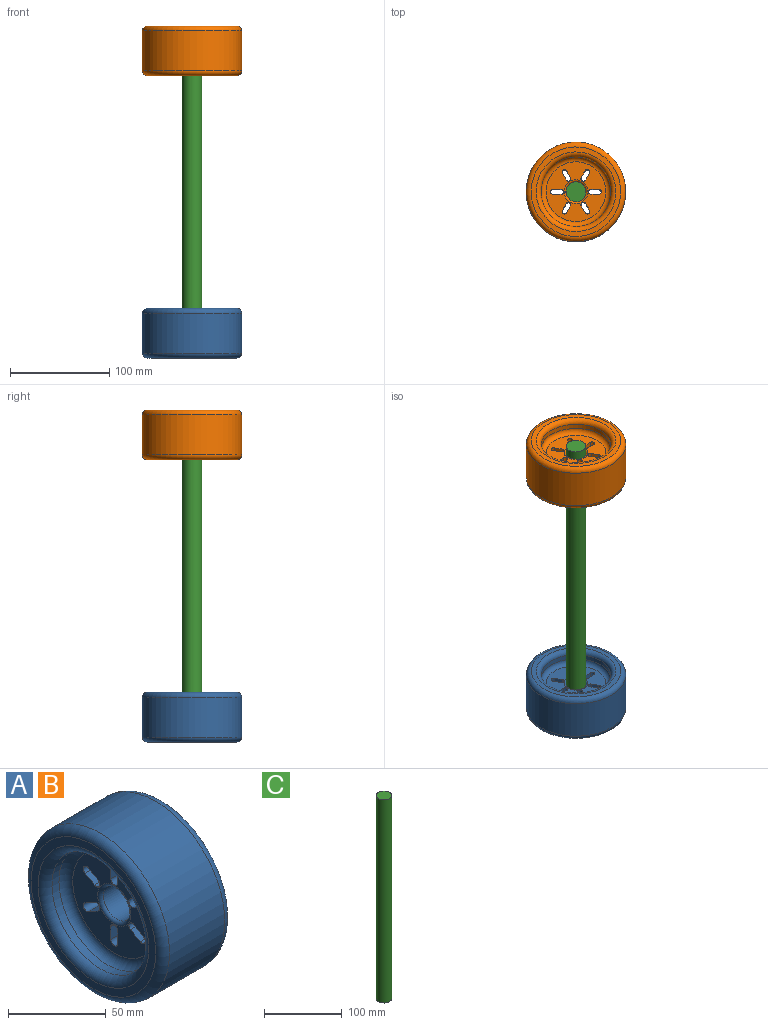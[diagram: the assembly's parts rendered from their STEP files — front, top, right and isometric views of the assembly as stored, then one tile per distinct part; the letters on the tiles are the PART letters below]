
ASSEMBLY  parts=3 mates=2
PART A: 89 faces, bbox 50.4x108.7x108.7 mm
  f0: plane 20.25x7.15mm, normal (0,0.5,0.87), area 160mm2, adj f1,f3,f20,f21
  f1: cylinder r=2.5mm len=20mm, axis (1,0,0), area 157.1mm2, adj f0,f2,f20,f21
  f2: plane 20.25x7.15mm, normal (0,-0.5,-0.87), area 160mm2, adj f1,f3,f20,f21
  f3: cylinder r=2.5mm len=20mm, axis (1,0,0), area 157.1mm2, adj f0,f2,f20,f21
  f4: plane 20.25x7.15mm, normal (0,-0.5,0.87), area 160mm2, adj f5,f7,f20,f21
  f5: cylinder r=2.5mm len=20mm, axis (1,0,0), area 157.1mm2, adj f4,f6,f20,f21
  f6: plane 20.25x7.15mm, normal (0,0.5,-0.87), area 160mm2, adj f5,f7,f20,f21
  f7: cylinder r=2.5mm len=20mm, axis (1,0,0), area 157.1mm2, adj f4,f6,f20,f21
  f8: plane 20.25x8.23mm, normal (0,-1,0), area 160mm2, adj f9,f11,f20,f21
  f9: cylinder r=2.5mm len=20mm, axis (1,0,0), area 157.1mm2, adj f8,f10,f20,f21
  f10: plane 20.25x8.23mm, normal (0,1,0), area 160mm2, adj f9,f11,f20,f21
  f11: cylinder r=2.5mm len=20mm, axis (1,0,0), area 157.1mm2, adj f8,f10,f20,f21
  f12: plane 20.25x7.15mm, normal (0,-0.5,-0.87), area 160mm2, adj f13,f15,f20,f21
  f13: cylinder r=2.5mm len=20mm, axis (1,0,0), area 157.1mm2, adj f12,f14,f20,f21
  f14: plane 20.25x7.15mm, normal (0,0.5,0.87), area 160mm2, adj f13,f15,f20,f21
  f15: cylinder r=2.5mm len=20mm, axis (1,0,0), area 157.1mm2, adj f12,f14,f20,f21
  f16: plane 20.25x7.15mm, normal (0,0.5,-0.87), area 160mm2, adj f17,f19,f20,f21
  f17: cylinder r=2.5mm len=20mm, axis (1,0,0), area 157.1mm2, adj f16,f18,f20,f21
  f18: plane 20.25x7.15mm, normal (0,-0.5,0.87), area 160mm2, adj f17,f19,f20,f21
  f19: cylinder r=2.5mm len=20mm, axis (1,0,0), area 157.1mm2, adj f16,f18,f20,f21
  f20: cone r=30.06mm half-angle=89.8deg, axis (-1,0,0), area 2018.5mm2, adj f0,f1,f2,f3,f4,f5,f6,f7
  f21: cone r=30.02mm half-angle=89.8deg, axis (-1,0,0), area 2010.6mm2, adj f0,f1,f2,f3,f4,f5,f6,f7
  f22: plane 90.08x90.08mm, normal (1,0,0), area 1336.4mm2, adj f23,f35
  f23: torus R=45.04mm, axis (-1,0,0), area 2379.7mm2, adj f22,f24
  f24: cylinder r=50.04mm len=100.08mm, axis (-1,0,0), area 12576.5mm2, adj f23,f25
  f25: torus R=45.04mm, axis (-1,0,0), area 2379.7mm2, adj f24,f26
  f26: plane 90.08x90.08mm, normal (-1,0,0), area 1336.4mm2, adj f25,f27
  f27: torus R=40.04mm, axis (-1,0,0), area 1818.8mm2, adj f26,f28
  f28: cylinder r=35.04mm len=70.08mm, axis (-1,0,0), area 1110.7mm2, adj f27,f29
  f29: torus R=30.04mm, axis (-1,0,0), area 1636.1mm2, adj f20,f28
  f30: torus R=12.04mm, axis (-1,0,0), area 212mm2, adj f20,f31
  f31: cylinder r=10.04mm len=20.08mm, axis (-1,0,0), area 1009.4mm2, adj f30,f32
  f32: torus R=12.04mm, axis (-1,0,0), area 213.1mm2, adj f21,f31
  f33: torus R=30.04mm, axis (-1,0,0), area 1642.9mm2, adj f21,f34
  f34: cylinder r=35.04mm len=70.08mm, axis (-1,0,0), area 1090.9mm2, adj f33,f35
  f35: torus R=40.04mm, axis (-1,0,0), area 1818.8mm2, adj f22,f34
  f36: cylinder r=2.5mm len=20.01mm, axis (1,0,0), area 157.1mm2, adj f20,f21,f37,f38
  f37: plane 20.25x8.23mm, normal (0,1,0), area 160mm2, adj f20,f21,f36,f39
  f38: plane 20.25x8.23mm, normal (0,-1,0), area 160mm2, adj f20,f21,f36,f39
  f39: cylinder r=2.5mm len=20.01mm, axis (1,0,0), area 157.1mm2, adj f20,f21,f37,f38
  f40: cone r=30.02mm half-angle=89.8deg, axis (-1,0,0), area 1586.8mm2, adj f41,f42,f43,f44,f45,f46,f47,f48
  f41: cylinder r=12.04mm len=16mm, axis (-1,0,0), area 104.3mm2, adj f40,f42,f62,f73
  f42: cylinder r=4.5mm len=16.01mm, axis (1,0,0), area 60.3mm2, adj f40,f41,f57,f73
  f43: cylinder r=12.04mm len=16mm, axis (-1,0,0), area 104.3mm2, adj f40,f44,f66,f73
  f44: cylinder r=4.5mm len=16.01mm, axis (1,0,0), area 60.3mm2, adj f40,f43,f61,f73
  f45: cylinder r=12.04mm len=16mm, axis (-1,0,0), area 104.3mm2, adj f40,f46,f70,f73
  f46: cylinder r=4.5mm len=16.01mm, axis (1,0,0), area 60.3mm2, adj f40,f45,f65,f73
  f47: cylinder r=12.04mm len=16mm, axis (-1,0,0), area 104.3mm2, adj f40,f48,f73,f85
  f48: cylinder r=4.5mm len=16.01mm, axis (1,0,0), area 60.3mm2, adj f40,f47,f69,f73
  f49: cylinder r=12.04mm len=16mm, axis (-1,0,0), area 104.3mm2, adj f40,f50,f53,f73
  f50: cylinder r=4.5mm len=16.01mm, axis (1,0,0), area 60.3mm2, adj f40,f49,f73,f86
  f51: cylinder r=12.04mm len=16mm, axis (-1,0,0), area 104.3mm2, adj f40,f52,f58,f73
  f52: cylinder r=4.5mm len=16.01mm, axis (1,0,0), area 60.3mm2, adj f40,f51,f54,f73
  f53: cylinder r=4.5mm len=16.01mm, axis (1,0,0), area 60.3mm2, adj f40,f49,f55,f73
  f54: plane 16.41x7.31mm, normal (0,-0.5,-0.87), area 128mm2, adj f40,f52,f56,f73
  f55: plane 16.41x7.31mm, normal (0,0.5,0.87), area 128mm2, adj f40,f53,f56,f73
  f56: cylinder r=4.5mm len=16mm, axis (1,0,0), area 226.2mm2, adj f40,f54,f55,f73
  f57: plane 16.41x7.31mm, normal (0,0.5,-0.87), area 128mm2, adj f40,f42,f60,f73
  f58: cylinder r=4.5mm len=16.01mm, axis (1,0,0), area 60.3mm2, adj f40,f51,f59,f73
  f59: plane 16.41x7.31mm, normal (0,-0.5,0.87), area 128mm2, adj f40,f58,f60,f73
  f60: cylinder r=4.5mm len=16mm, axis (1,0,0), area 226.2mm2, adj f40,f57,f59,f73
  f61: plane 16.41x8.38mm, normal (0,1,0), area 128mm2, adj f40,f44,f64,f73
  f62: cylinder r=4.5mm len=16.01mm, axis (1,0,0), area 60.3mm2, adj f40,f41,f63,f73
  f63: plane 16.41x8.38mm, normal (0,-1,0), area 128mm2, adj f40,f62,f64,f73
  f64: cylinder r=4.5mm len=16mm, axis (1,0,0), area 226.2mm2, adj f40,f61,f63,f73
  f65: plane 16.41x7.31mm, normal (0,0.5,0.87), area 128mm2, adj f40,f46,f68,f73
  f66: cylinder r=4.5mm len=16.01mm, axis (1,0,0), area 60.3mm2, adj f40,f43,f67,f73
  f67: plane 16.41x7.31mm, normal (0,-0.5,-0.87), area 128mm2, adj f40,f66,f68,f73
  f68: cylinder r=4.5mm len=16mm, axis (1,0,0), area 226.2mm2, adj f40,f65,f67,f73
  f69: plane 16.41x7.31mm, normal (0,-0.5,0.87), area 128mm2, adj f40,f48,f72,f73
  f70: cylinder r=4.5mm len=16.01mm, axis (1,0,0), area 60.3mm2, adj f40,f45,f71,f73
  f71: plane 16.41x7.31mm, normal (0,0.5,-0.87), area 128mm2, adj f40,f70,f72,f73
  f72: cylinder r=4.5mm len=16mm, axis (1,0,0), area 226.2mm2, adj f40,f69,f71,f73
  f73: cone r=30.07mm half-angle=89.8deg, axis (-1,0,0), area 1596.2mm2, adj f41,f42,f43,f44,f45,f46,f47,f48
  f74: plane 90.08x90.08mm, normal (-1,0,0), area 1336.4mm2, adj f75,f84
  f75: torus R=45.04mm, axis (-1,0,0), area 1390.1mm2, adj f74,f76
  f76: cylinder r=48.04mm len=96.08mm, axis (-1,0,0), area 12073.8mm2, adj f75,f77
  f77: torus R=45.04mm, axis (-1,0,0), area 1390.1mm2, adj f76,f78
  f78: plane 90.08x90.08mm, normal (1,0,0), area 1336.4mm2, adj f77,f79
  f79: torus R=40.04mm, axis (-1,0,0), area 1129mm2, adj f78,f80
  f80: cylinder r=37.04mm len=74.08mm, axis (-1,0,0), area 1174.1mm2, adj f79,f81
  f81: torus R=30.04mm, axis (-1,0,0), area 2378.5mm2, adj f73,f80
  f82: torus R=30.04mm, axis (-1,0,0), area 2388mm2, adj f40,f83
  f83: cylinder r=37.04mm len=74.08mm, axis (-1,0,0), area 1153.1mm2, adj f82,f84
  f84: torus R=40.04mm, axis (-1,0,0), area 1129mm2, adj f74,f83
  f85: cylinder r=4.5mm len=16.01mm, axis (1,0,0), area 60.3mm2, adj f40,f47,f73,f87
  f86: plane 16.41x8.38mm, normal (0,-1,0), area 128mm2, adj f40,f50,f73,f88
  f87: plane 16.41x8.38mm, normal (0,1,0), area 128mm2, adj f40,f73,f85,f88
  f88: cylinder r=4.5mm len=16.01mm, axis (1,0,0), area 226.2mm2, adj f40,f73,f86,f87
PART B: same geometry as A
PART C: 3 faces, bbox 20x20x320 mm
  f0: cylinder r=10mm len=320mm, axis (0,0,-1), area 20106.2mm2, adj f1,f2
  f1: plane 20x20mm, normal (0,0,1), area 314.2mm2, adj f0
  f2: plane 20x20mm, normal (0,0,-1), area 314.2mm2, adj f0
PLACE A rot(axis=(0,1,0),90deg) t=(-205.92,104.65,-108.25)mm
PLACE B rot(axis=(0,1,0),90deg) t=(-205.92,104.65,175.75)mm
PLACE C t=(-248.46,104.65,-126.36)mm fixed
MATE fastened A.f23 <-> C.f0  axis (0,0,1) through (-248.46,104.65,-116.36)mm
MATE fastened B.f23 <-> C.f0  axis (0,0,1) through (-248.46,104.65,183.64)mm
